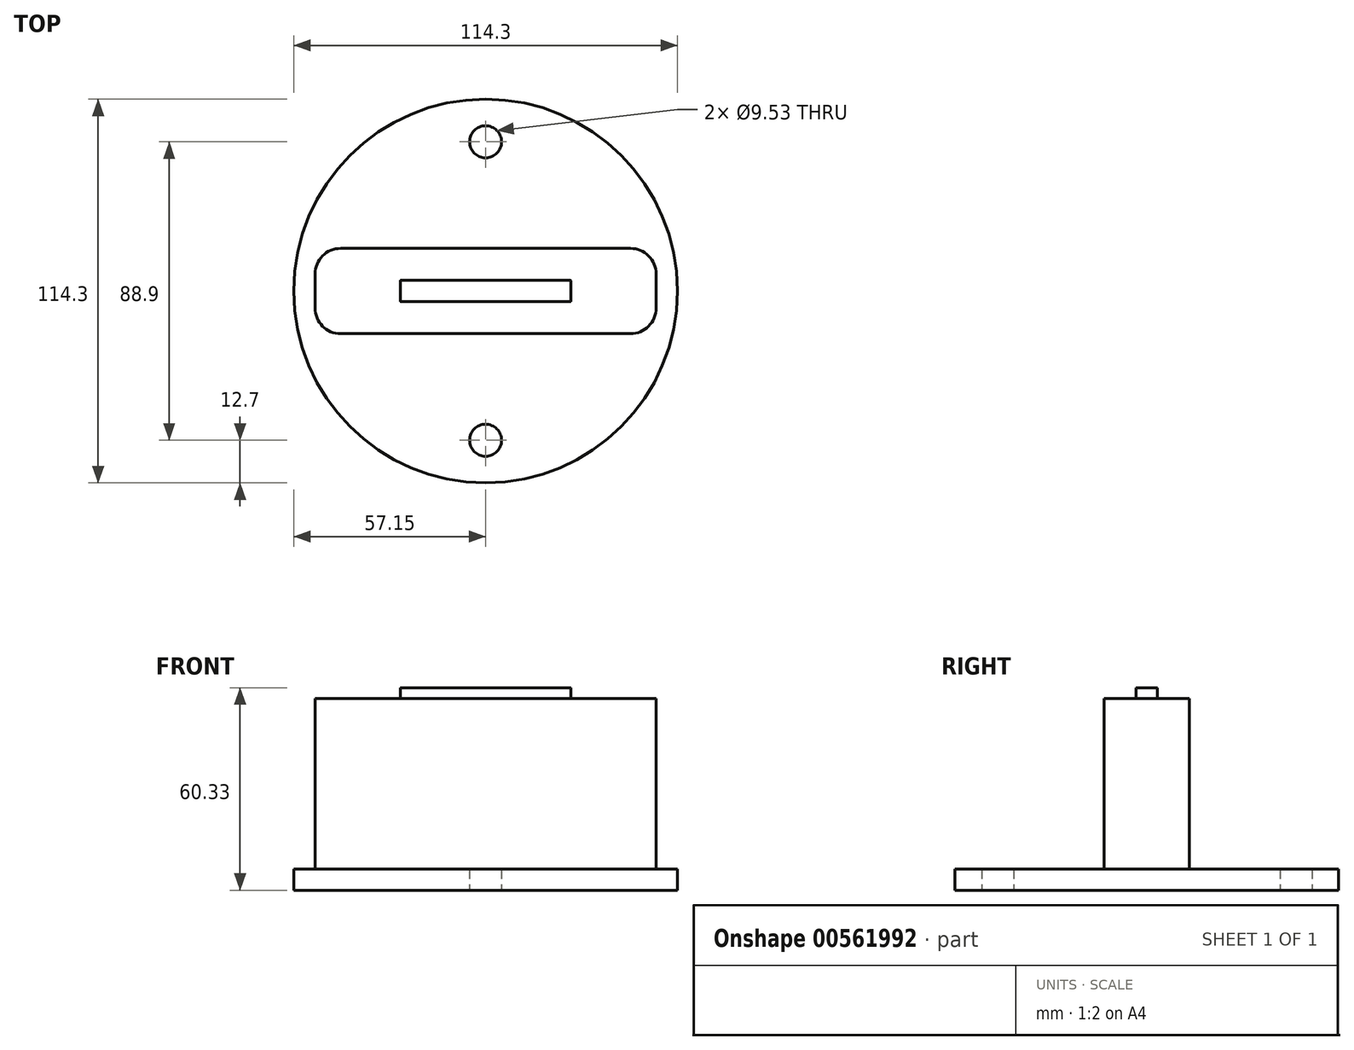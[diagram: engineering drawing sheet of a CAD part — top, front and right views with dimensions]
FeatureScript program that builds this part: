
annotation { "Feature Type Name" : "Feature", "Feature Type Description" : "" }
export const myFeature = defineFeature(function(context is Context, id is Id, definition is map)
    precondition{}
    {
        {
            var Q0;
            Q0=qCreatedBy(makeId("Top.planeOp"),FACE);
            var sketch = newSketch(context, id + "F0", { "sketchPlane" : qUnion([Q0])});
            skLineSegment(sketch, "E0.bottom", {"start": v(-50.8, 12.7) * mm, "end": v(50.8, 12.7) * mm});
            skLineSegment(sketch, "E0.top", {"start": v(-50.8, -12.7) * mm, "end": v(50.8, -12.7) * mm});
            skLineSegment(sketch, "E0.left", {"start": v(-50.8, 12.7) * mm, "end": v(-50.8, -12.7) * mm});
            skLineSegment(sketch, "E0.right", {"start": v(50.8, 12.7) * mm, "end": v(50.8, -12.7) * mm});
            skPoint(sketch, "E0.middle", {"position": v(0, 0) * mm});
            skSolve(sketch);
        }
        {
            var Q0;
            Q0 = qSketchRegion(id + "F0", true);
            extrude(context, id + "F1", {"entities" : qUnion([Q0]), "depth" : 50.8 * mm, "offsetDistance" : 25.4 * mm});
        }
        {
            var Q0;
            Q0=makeQuery(id+"F1.opExtrude","CAP_FACE",FACE,{"disambiguationData":[OSD([sQuery(id+"F0.wireOp",EDGE,"E0.bottom"),sQuery(id+"F0.wireOp",EDGE,"E0.top"),sQuery(id+"F0.wireOp",EDGE,"E0.left"),sQuery(id+"F0.wireOp",EDGE,"E0.right")])],"isStart":false});
            var sketch = newSketch(context, id + "F2", { "sketchPlane" : qUnion([Q0])});
            skLineSegment(sketch, "E1.bottom", {"start": v(-25.4, 3.17) * mm, "end": v(25.4, 3.17) * mm});
            skLineSegment(sketch, "E1.top", {"start": v(-25.4, -3.17) * mm, "end": v(25.4, -3.17) * mm});
            skLineSegment(sketch, "E1.left", {"start": v(-25.4, 3.17) * mm, "end": v(-25.4, -3.17) * mm});
            skLineSegment(sketch, "E1.right", {"start": v(25.4, 3.17) * mm, "end": v(25.4, -3.17) * mm});
            skPoint(sketch, "E1.middle", {"position": v(0, 0) * mm});
            skSolve(sketch);
        }
        {
            var Q0;
            Q0 = qSketchRegion(id + "F2", true);
            extrude(context, id + "F3", {"entities" : qUnion([Q0]), "operationType" : NewBodyOperationType.ADD, "depth" : 3.17 * mm, "offsetDistance" : 25.4 * mm});
        }
        {
            var Q0;
            Q0=makeQuery(id+"F1.opExtrude","CAP_FACE",FACE,{"disambiguationData":[OSD([sQuery(id+"F0.wireOp",EDGE,"E0.bottom"),sQuery(id+"F0.wireOp",EDGE,"E0.top"),sQuery(id+"F0.wireOp",EDGE,"E0.left"),sQuery(id+"F0.wireOp",EDGE,"E0.right")])],"isStart":true});
            var sketch = newSketch(context, id + "F4", { "sketchPlane" : qUnion([Q0])});
            skCircle(sketch, "E2", {"center": v(0, 0) * mm, "radius": 57.15 * mm});
            skSolve(sketch);
        }
        {
            var Q0;
            Q0 = qSketchRegion(id + "F4", true);
            extrude(context, id + "F5", {"entities" : qUnion([Q0]), "operationType" : NewBodyOperationType.ADD, "depth" : 6.35 * mm, "offsetDistance" : 25.4 * mm});
        }
        {
            var Q0;
            Q0=makeQuery(id+"F5.opExtrude","CAP_FACE",FACE,{"disambiguationData":[OSD([sQuery(id+"F4.wireOp",EDGE,"E2")])],"isStart":false});
            var sketch = newSketch(context, id + "F6", { "sketchPlane" : qUnion([Q0])});
            skCircle(sketch, "E3", {"center": v(0, 44.45) * mm, "radius": 4.76 * mm});
            skCircle(sketch, "E4", {"center": v(0, -44.45) * mm, "radius": 4.76 * mm});
            skSolve(sketch);
        }
        {
            var Q0;
            Q0 = qSketchRegion(id + "F6", true);
            extrude(context, id + "F7", {"entities" : qUnion([Q0]), "operationType" : NewBodyOperationType.REMOVE, "oppositeDirection" : true, "depth" : 25.4 * mm, "offsetDistance" : 25.4 * mm});
        }
        {
            var Q0;
            Q0=makeQuery(id+"F1.opExtrude","SWEPT_EDGE",EDGE,{"disambiguationData":[OSD([sQuery(id+"F0.wireOp",EDGE,"E0.top"),sQuery(id+"F0.wireOp",EDGE,"E0.right")])]});
            var Q1;
            Q1=makeQuery(id+"F1.opExtrude","SWEPT_EDGE",EDGE,{"disambiguationData":[OSD([sQuery(id+"F0.wireOp",EDGE,"E0.bottom"),sQuery(id+"F0.wireOp",EDGE,"E0.right")])]});
            var Q2;
            Q2=makeQuery(id+"F1.opExtrude","SWEPT_EDGE",EDGE,{"disambiguationData":[OSD([sQuery(id+"F0.wireOp",EDGE,"E0.top"),sQuery(id+"F0.wireOp",EDGE,"E0.left")])]});
            var Q3;
            Q3=makeQuery(id+"F1.opExtrude","SWEPT_EDGE",EDGE,{"disambiguationData":[OSD([sQuery(id+"F0.wireOp",EDGE,"E0.bottom"),sQuery(id+"F0.wireOp",EDGE,"E0.left")])]});
            fillet(context, id + "F8", {"entities" : qUnion([Q0, Q1, Q2, Q3]), "radius" : 7.62 * mm, "tangentPropagation" : true, "allowEdgeOverflow" : false});
        }
        {
            var Q0;
            Q0=makeQuery(id+"F3.opExtrude","CAP_FACE",FACE,{"disambiguationData":[OSD([sQuery(id+"F2.wireOp",EDGE,"E1.bottom"),sQuery(id+"F2.wireOp",EDGE,"E1.top"),sQuery(id+"F2.wireOp",EDGE,"E1.left"),sQuery(id+"F2.wireOp",EDGE,"E1.right")])],"isStart":false});
            var Q1;
            Q1=makeQuery(id+"F3.opExtrude","SWEPT_EDGE",EDGE,{"disambiguationData":[OSD([sQuery(id+"F2.wireOp",EDGE,"E1.top"),sQuery(id+"F2.wireOp",EDGE,"E1.right")])]});
            var Q2;
            Q2=makeQuery(id+"F3.opExtrude","SWEPT_EDGE",EDGE,{"disambiguationData":[OSD([sQuery(id+"F2.wireOp",EDGE,"E1.bottom"),sQuery(id+"F2.wireOp",EDGE,"E1.right")])]});
            var Q3;
            Q3=makeQuery(id+"F3.opExtrude","SWEPT_EDGE",EDGE,{"disambiguationData":[OSD([sQuery(id+"F2.wireOp",EDGE,"E1.top"),sQuery(id+"F2.wireOp",EDGE,"E1.left")])]});
            var Q4;
            Q4=makeQuery(id+"F3.opExtrude","SWEPT_EDGE",EDGE,{"disambiguationData":[OSD([sQuery(id+"F2.wireOp",EDGE,"E1.bottom"),sQuery(id+"F2.wireOp",EDGE,"E1.left")])]});
            fillet(context, id + "F9", {"entities" : qUnion([Q0, Q1, Q2, Q3, Q4]), "radius" : 0.13 * mm, "tangentPropagation" : true, "allowEdgeOverflow" : false});
        }
    });
